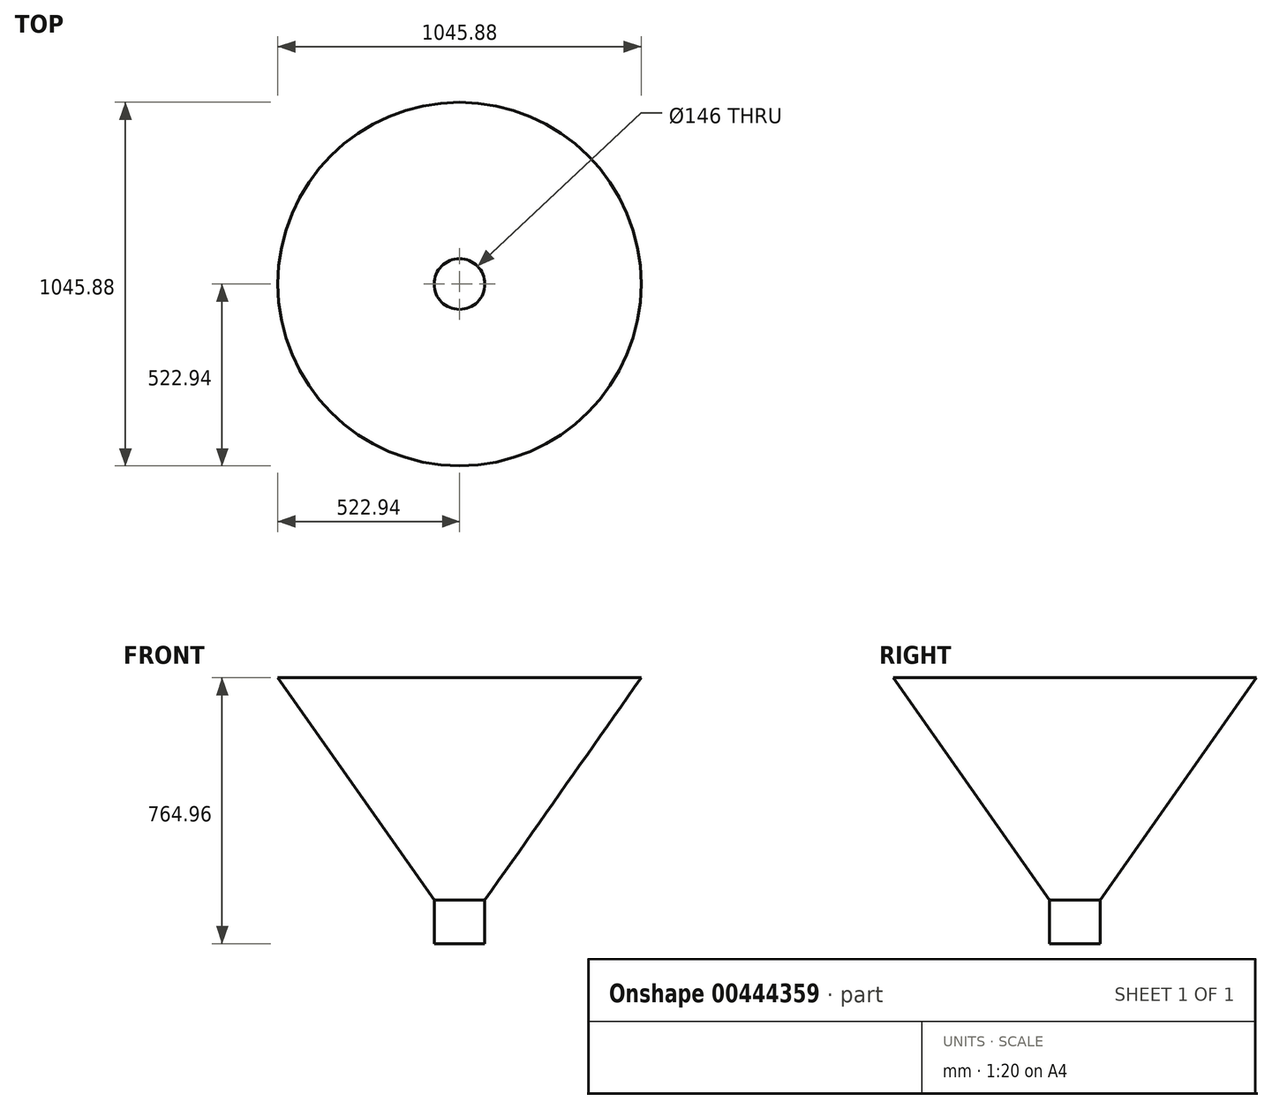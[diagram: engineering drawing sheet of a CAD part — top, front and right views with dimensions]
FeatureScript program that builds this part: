
annotation { "Feature Type Name" : "Feature", "Feature Type Description" : "" }
export const myFeature = defineFeature(function(context is Context, id is Id, definition is map)
    precondition{}
    {
        {
            var Q0;
            Q0=qCreatedBy(makeId("Front.planeOp"),FACE);
            var sketch = newSketch(context, id + "F0", { "sketchPlane" : qUnion([Q0])});
            skLineSegment(sketch, "E0", {"start": v(0, 0) * mm, "end": v(449.94, 639.96) * mm});
            skLineSegment(sketch, "E1", {"start": v(0, 0) * mm, "end": v(639.53, 0) * mm});
            skLineSegment(sketch, "E2", {"start": v(0, 0) * mm, "end": v(0, 123.99) * mm});
            skSolve(sketch);
        }
        {
            var Q0;
            Q0=qCreatedBy(makeId("Top.planeOp"),FACE);
            var sketch = newSketch(context, id + "F1", { "sketchPlane" : qUnion([Q0])});
            skLineSegment(sketch, "E3", {"start": v(0, 0) * mm, "end": v(0, 304.75) * mm});
            skCircle(sketch, "E4", {"center": v(-73, 0) * mm, "radius": 73 * mm});
            skSolve(sketch);
        }
        {
            var Q0;
            Q0=sQuery(id+"F0.wireOp",EDGE,"E0");
            var Q1;
            Q1=sQuery(id+"F1.wireOp",EDGE,"E4");
            revolve(context, id + "F2", {"bodyType" : ToolBodyType.SURFACE, "surfaceEntities" : qUnion([Q0]), "axis" : qUnion([Q1]), "revolveType" : RevolveType.FULL});
        }
        {
            var Q0;
            Q0=qCreatedBy(makeId("Right.planeOp"),FACE);
            var sketch = newSketch(context, id + "F3", { "sketchPlane" : qUnion([Q0])});
            skLineSegment(sketch, "E5", {"start": v(0, 0) * mm, "end": v(0, -125) * mm});
            skSolve(sketch);
        }
        {
            var Q0;
            Q0 = qSketchRegion(id + "F3", true);
            var Q1;
            Q1=makeQuery(id+"F1.imprint","IMPRINT",FACE,{"disambiguationData":[TD([[makeQuery(id+"F1.imprint","IMPRINT",EDGE,{"derivedFrom":sQuery(id+"F1.wireOp",EDGE,"E4")}),1.0]])]});
            var Q2;
            Q2=sQuery(id+"F1.wireOp",EDGE,"E4");
            var Q3;
            Q3=sQuery(id+"F3.wireOp",VERTEX,"E5.end");
            extrude(context, id + "F4", {"entities" : qUnion([Q0, Q1]), "bodyType" : ToolBodyType.SURFACE, "surfaceEntities" : qUnion([Q2]), "endBound" : BoundingType.UP_TO_VERTEX, "oppositeDirection" : true, "endBoundEntityVertex" : qUnion([Q3]), "depth" : 25 * mm});
        }
    });
